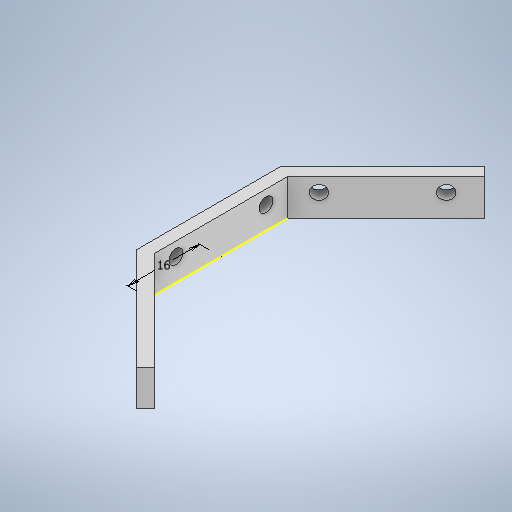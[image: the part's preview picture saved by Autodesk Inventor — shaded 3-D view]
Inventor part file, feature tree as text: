
AUTODESK INVENTOR PART (.ipt)
format: ipt  version: 2025.1 (Build 291241020, 241B)  size: 318,464 bytes
history: native  units: in
note: dims shown in document units (in); Inventor stores cm internally (conversion verified against a paired STEP export)
features: sketch x5, extrude x4
ambient origin geometry x8: Origin, YZ Plane, XZ Plane, XY Plane, X Axis, Y Axis, Z Axis, Center Point
bodies: Body1 (feature_tree)
feature tree (9):
  extrude  "Extrusion2"  Depth=0.315in
  extrude  "Extrusion7"  Depth=0.0787in
  extrude  "Extrusion8"  Depth=1.2205in
  extrude  "Extrusion9"  Depth=0.5118in
  sketch  "Sketch12"  dims[d74=0.1181in d75=0.1969in d76=0.3937in d77=0.1201in d78=0.1201in d79=0.315in d80=0.0in d81=0.5118in d82=0.1181in d83=0.1969in d84=0.3937in d85=0.1201in d86=0.1201in d87=0.315in d88=0.0in d89=0.6299in d90=0.5118in d91=0.1181in d92=0.1969in d93=0.3937in d94=0.1201in d95=0.1201in d96=0.315in d97=0.0in d98=0.6299in d14=0.0197in d15=0.0344in d16=0.0197in d17=0.0344in]
  sketch  "Sketch1"  dims[d18=0.315in d19=0.0in d64=1.2598in]
  sketch  "Sketch9"  dims[d65=1.2598in d66=0.0787in]
  sketch  "Sketch10"  dims[d67=1.2598in d70=1.2205in]
  sketch  "Sketch11"  dims[d72=0.6299in d73=0.5118in]
